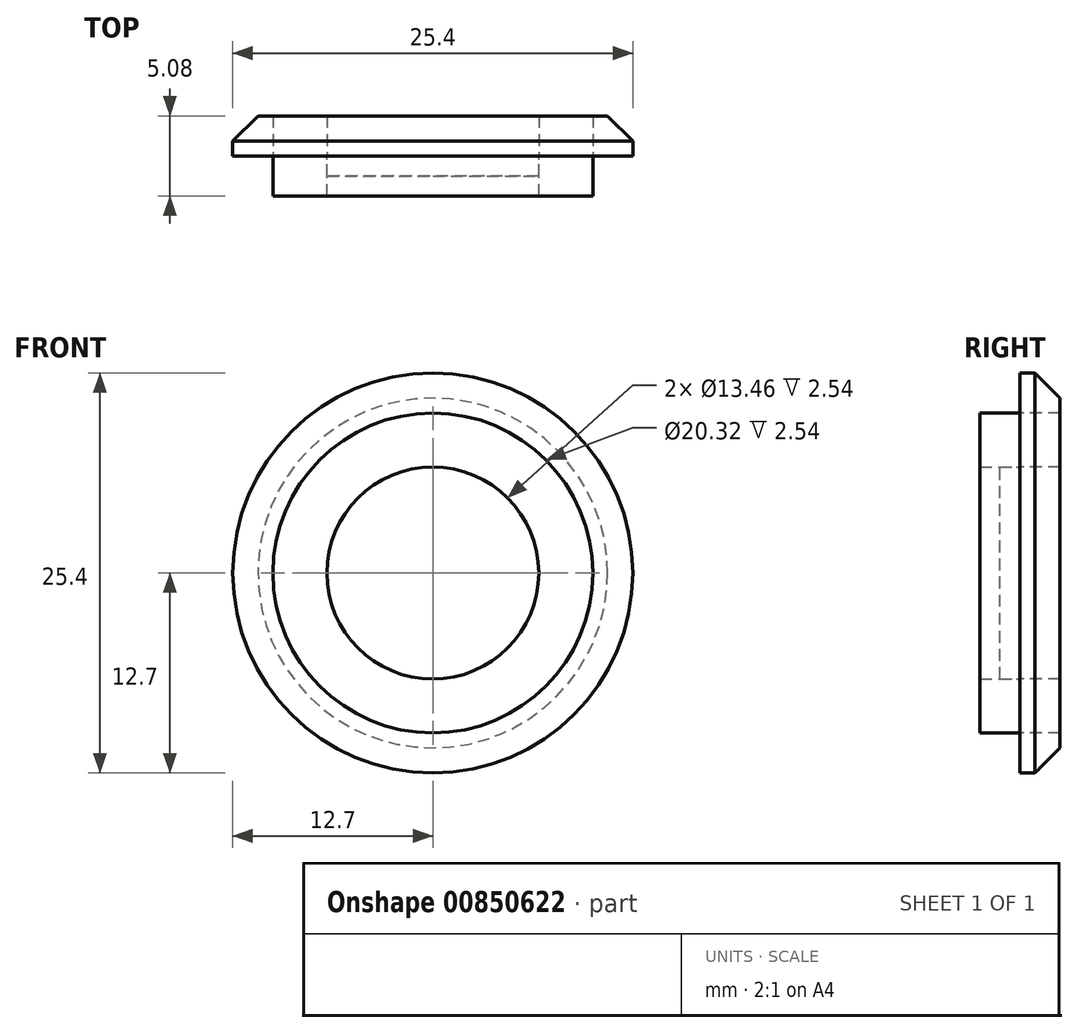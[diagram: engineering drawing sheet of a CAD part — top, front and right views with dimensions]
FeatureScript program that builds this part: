
annotation { "Feature Type Name" : "Feature", "Feature Type Description" : "" }
export const myFeature = defineFeature(function(context is Context, id is Id, definition is map)
    precondition{}
    {
        {
            var Q0;
            Q0=qCreatedBy(makeId("Front.planeOp"),FACE);
            var sketch = newSketch(context, id + "F0", { "sketchPlane" : qUnion([Q0])});
            skCircle(sketch, "E0", {"center": v(0, 0) * mm, "radius": 6.73 * mm});
            skCircle(sketch, "E1", {"center": v(0, 0) * mm, "radius": 10.16 * mm});
            skCircle(sketch, "E2", {"center": v(0, 0) * mm, "radius": 12.7 * mm});
            skSolve(sketch);
        }
        {
            var Q0;
            Q0=makeQuery(id+"F0.imprint","IMPRINT",FACE,{"disambiguationData":[TD([[makeQuery(id+"F0.imprint","IMPRINT",EDGE,{"derivedFrom":sQuery(id+"F0.wireOp",EDGE,"E0")}),-1.0]])]});
            var Q1;
            Q1=sQuery(id+"F0.wireOp",EDGE,"E1");
            extrude(context, id + "F1", {"entities" : qUnion([Q0]), "surfaceEntities" : qUnion([Q1]), "depth" : 2.54 * mm, "offsetDistance" : 25.4 * mm});
        }
        {
            var Q0;
            Q0=makeQuery(id+"F0.imprint","IMPRINT",FACE,{"disambiguationData":[TD([[makeQuery(id+"F0.imprint","IMPRINT",EDGE,{"derivedFrom":sQuery(id+"F0.wireOp",EDGE,"E0")}),1.0]])]});
            var Q1;
            Q1=sQuery(id+"F0.wireOp",EDGE,"E0");
            extrude(context, id + "F2", {"entities" : qUnion([Q0]), "surfaceEntities" : qUnion([Q1]), "depth" : 1.27 * mm, "offsetDistance" : 25.4 * mm});
        }
        {
            var Q0;
            Q0=makeQuery(id+"F0.imprint","IMPRINT",FACE,{"disambiguationData":[TD([[makeQuery(id+"F0.imprint","IMPRINT",EDGE,{"derivedFrom":sQuery(id+"F0.wireOp",EDGE,"E1")}),-1.0]])]});
            var Q1;
            Q1=sQuery(id+"F0.wireOp",EDGE,"E2");
            extrude(context, id + "F3", {"entities" : qUnion([Q0]), "surfaceEntities" : qUnion([Q1]), "oppositeDirection" : true, "depth" : 2.54 * mm, "offsetDistance" : 25.4 * mm});
        }
        {
            var Q0;
            Q0=makeQuery(id+"F0.imprint","IMPRINT",FACE,{"disambiguationData":[TD([[makeQuery(id+"F0.imprint","IMPRINT",EDGE,{"derivedFrom":sQuery(id+"F0.wireOp",EDGE,"E0")}),-1.0]])]});
            extrude(context, id + "F4", {"entities" : qUnion([Q0]), "oppositeDirection" : true, "depth" : 2.54 * mm, "offsetDistance" : 25.4 * mm});
        }
        {
            var Q0;
            Q0=makeQuery(id+"F0.imprint","IMPRINT",FACE,{"disambiguationData":[TD([[makeQuery(id+"F0.imprint","IMPRINT",EDGE,{"derivedFrom":sQuery(id+"F0.wireOp",EDGE,"E0")}),1.0]])]});
            var Q1;
            Q1=sQuery(id+"F0.wireOp",EDGE,"E0");
            extrude(context, id + "F5", {"entities" : qUnion([Q0]), "surfaceEntities" : qUnion([Q1]), "oppositeDirection" : true, "depth" : 2.54 * mm, "offsetDistance" : 25.4 * mm});
        }
        {
            var Q0;
            Q0=makeQuery(id+"F3.opExtrude","CAP_EDGE",EDGE,{"disambiguationData":[OSD([sQuery(id+"F0.wireOp",EDGE,"E2")])],"isStart":false});
            chamfer(context, id + "F6", {"entities" : qUnion([Q0]), "width" : 1.6 * mm, "tangentPropagation" : true});
        }
    });
